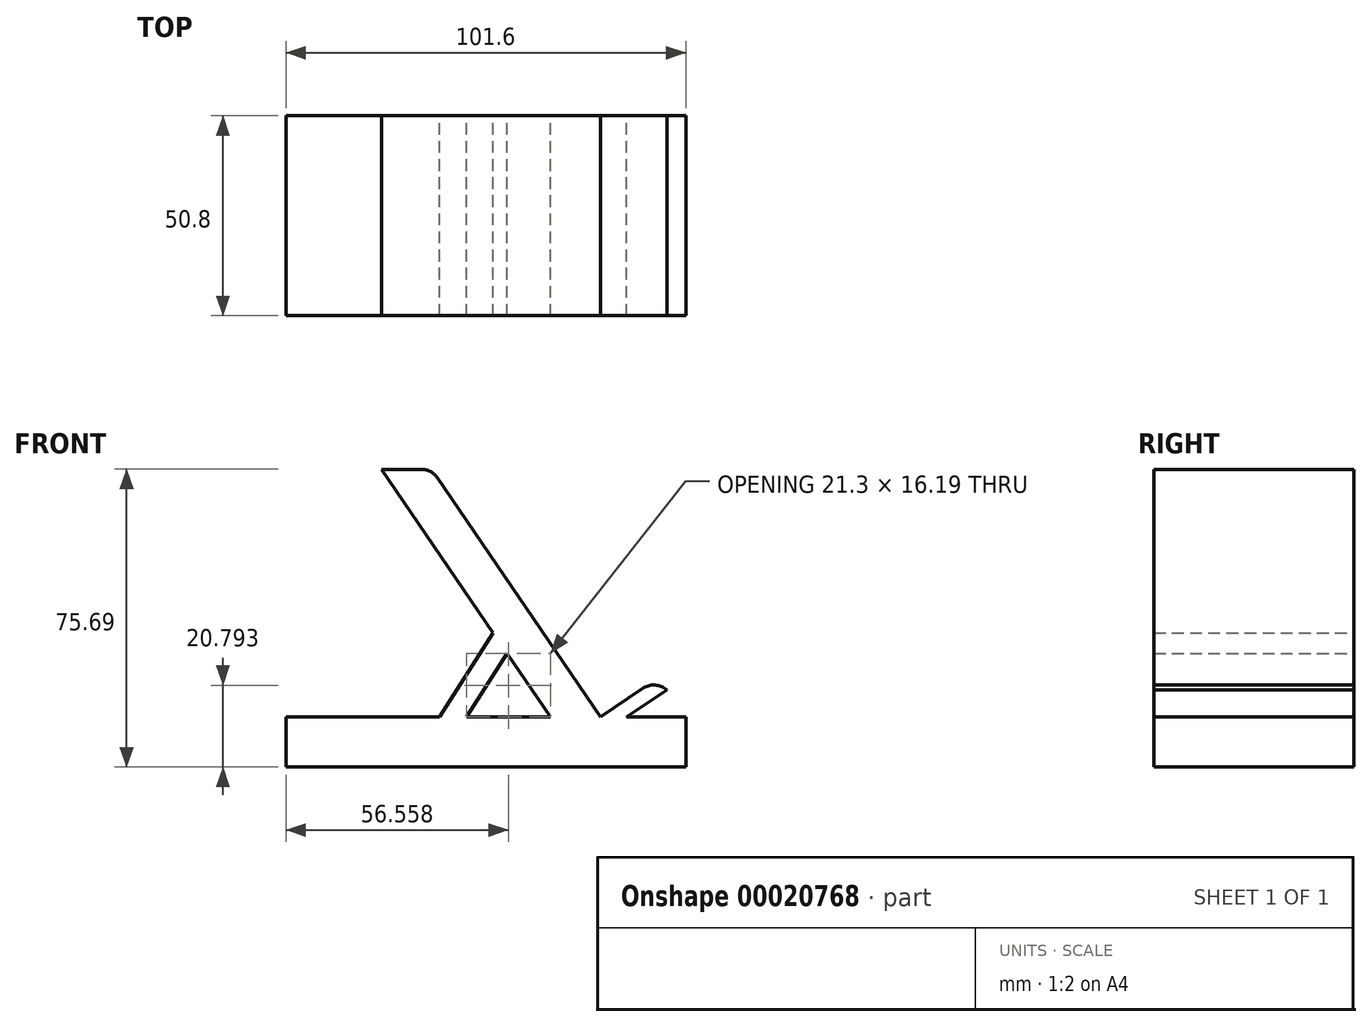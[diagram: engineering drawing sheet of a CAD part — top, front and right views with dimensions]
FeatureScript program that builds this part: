
annotation { "Feature Type Name" : "Feature", "Feature Type Description" : "" }
export const myFeature = defineFeature(function(context is Context, id is Id, definition is map)
    precondition{}
    {
        {
            var Q0;
            Q0=qCreatedBy(makeId("Front.planeOp"),FACE);
            var sketch = newSketch(context, id + "F0", { "sketchPlane" : qUnion([Q0])});
            skLineSegment(sketch, "E0.bottom", {"start": v(-52.74, -22.8) * mm, "end": v(48.86, -22.8) * mm});
            skLineSegment(sketch, "E0.top", {"start": v(-52.74, -10.1) * mm, "end": v(14.47, -10.1) * mm});
            skLineSegment(sketch, "E0.left", {"start": v(-52.74, -22.8) * mm, "end": v(-52.74, -10.1) * mm});
            skLineSegment(sketch, "E0.right", {"start": v(48.86, -22.8) * mm, "end": v(48.86, -10.1) * mm});
            skLineSegment(sketch, "E1", {"start": v(14.47, -10.1) * mm, "end": v(3.45, 6.1) * mm});
            skLineSegment(sketch, "E2", {"start": v(27.17, -10.1) * mm, "end": v(-15.71, 52.9) * mm});
            skLineSegment(sketch, "E3", {"start": v(-28.41, 52.9) * mm, "end": v(-15.71, 52.9) * mm});
            skLineSegment(sketch, "E4.trimOffspring", {"start": v(33.87, -10.1) * mm, "end": v(48.86, -10.1) * mm});
            skLineSegment(sketch, "E5", {"start": v(27.17, -10.1) * mm, "end": v(42, 0) * mm});
            skLineSegment(sketch, "E6", {"start": v(33.87, -10.1) * mm, "end": v(44.03, -3.17) * mm});
            skLineSegment(sketch, "E7", {"start": v(42, 0) * mm, "end": v(44.03, -3.17) * mm});
            skLineSegment(sketch, "E8", {"start": v(-13.74, -10.1) * mm, "end": v(-0.13, 11.35) * mm});
            skLineSegment(sketch, "E9", {"start": v(-6.83, -10.1) * mm, "end": v(3.45, 6.1) * mm});
            skLineSegment(sketch, "E10.trimOffspring", {"start": v(-0.13, 11.35) * mm, "end": v(-28.41, 52.9) * mm});
            skSolve(sketch);
        }
        {
            var Q0;
            Q0=makeQuery(id+"F0.imprint","IMPRINT",FACE,{"disambiguationData":[TD([[makeQuery(id+"F0.imprint","IMPRINT",EDGE,{"derivedFrom":sQuery(id+"F0.wireOp",EDGE,"E0.bottom")}),1.0]])]});
            extrude(context, id + "F1", {"entities" : qUnion([Q0]), "depth" : 50.8 * mm});
        }
        {
            var Q0;
            Q0=makeQuery(id+"F1.opExtrude","SWEPT_EDGE",EDGE,{"disambiguationData":[OSD([sQuery(id+"F0.wireOp",EDGE,"E5"),sQuery(id+"F0.wireOp",EDGE,"E7")])]});
            var Q1;
            Q1=makeQuery(id+"F1.opExtrude","SWEPT_EDGE",EDGE,{"disambiguationData":[OSD([sQuery(id+"F0.wireOp",EDGE,"E2"),sQuery(id+"F0.wireOp",EDGE,"E3")])]});
            fillet(context, id + "F2", {"entities" : qUnion([Q0, Q1]), "radius" : 5.08 * mm, "tangentPropagation" : true, "allowEdgeOverflow" : false});
        }
    });
